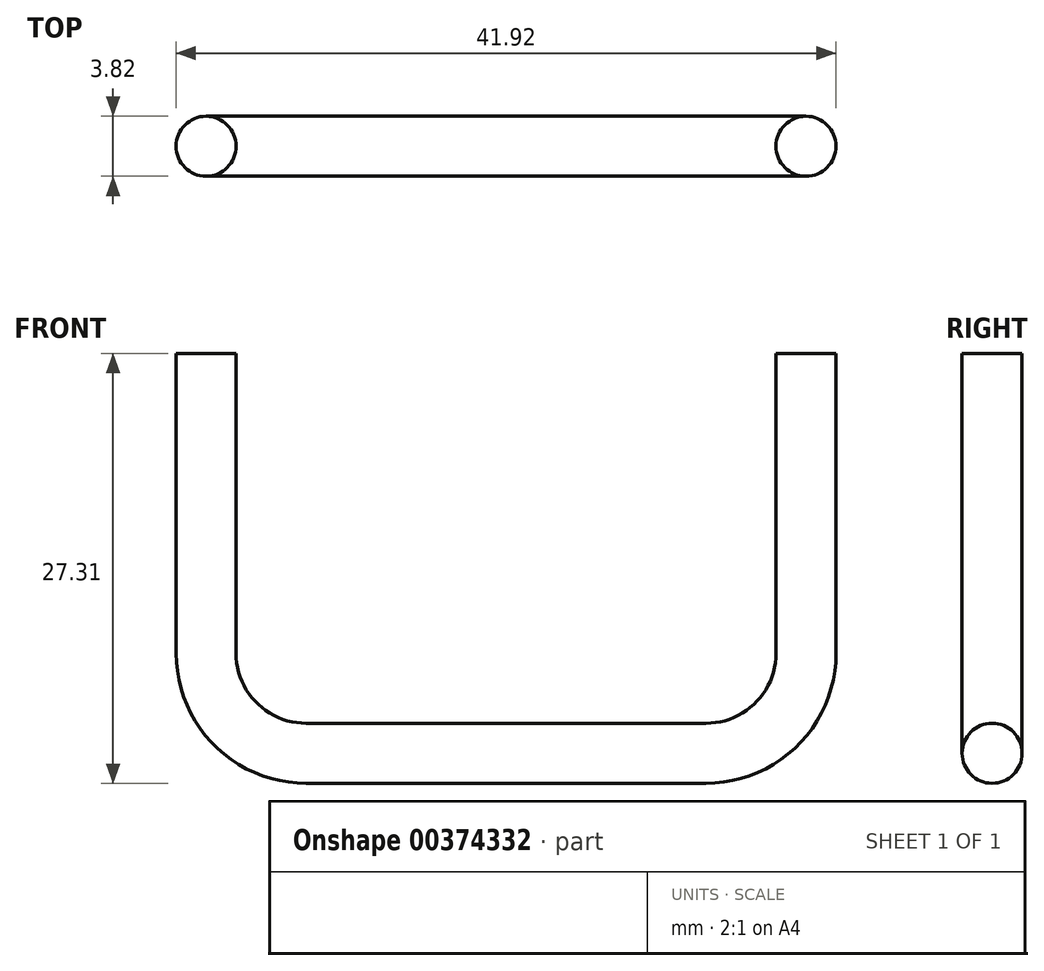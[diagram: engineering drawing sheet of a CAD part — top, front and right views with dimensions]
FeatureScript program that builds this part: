
annotation { "Feature Type Name" : "Feature", "Feature Type Description" : "" }
export const myFeature = defineFeature(function(context is Context, id is Id, definition is map)
    precondition{}
    {
        {
            var Q0;
            Q0=qCreatedBy(makeId("Front.planeOp"),FACE);
            var sketch = newSketch(context, id + "F0", { "sketchPlane" : qUnion([Q0])});
            skLineSegment(sketch, "E0", {"start": v(-19.05, 0) * mm, "end": v(-19.05, -19.05) * mm});
            skLineSegment(sketch, "E1", {"start": v(-12.7, -25.4) * mm, "end": v(12.7, -25.4) * mm});
            skLineSegment(sketch, "E2", {"start": v(19.05, -19.05) * mm, "end": v(19.05, 0) * mm});
            skPoint(sketch, "E3.visualSharp", {"position": v(-19.05, -25.4) * mm});
            skArc(sketch, "E3.filletArc", {"start": v(-19.05, -19.05) * mm, "mid": v(-17.2, -23.54) * mm, "end": v(-12.7, -25.4) * mm});
            skPoint(sketch, "E4.visualSharp", {"position": v(19.05, -25.4) * mm});
            skArc(sketch, "E4.filletArc", {"start": v(12.7, -25.4) * mm, "mid": v(17.2, -23.54) * mm, "end": v(19.05, -19.05) * mm});
            skSolve(sketch);
        }
        {
            var Q0;
            Q0=qCreatedBy(makeId("Top.planeOp"),FACE);
            var sketch = newSketch(context, id + "F1", { "sketchPlane" : qUnion([Q0])});
            skCircle(sketch, "E5", {"center": v(-19.05, 0) * mm, "radius": 1.9 * mm});
            skSolve(sketch);
        }
        {
            var Q0;
            Q0=makeQuery(id+"F1.imprint","IMPRINT",FACE,{"disambiguationData":[TD([[makeQuery(id+"F1.imprint","IMPRINT",EDGE,{"derivedFrom":sQuery(id+"F1.wireOp",EDGE,"E5")}),1.0]])]});
            var Q1;
            Q1 = qConstructionFilter(qBodyType(qCreatedBy(id + "F0" ,EDGE), BodyType.WIRE), ConstructionObject.NO);
            sweep(context, id + "F2", {"profiles" : qUnion([Q0]), "path" : qUnion([Q1])});
        }
    });
